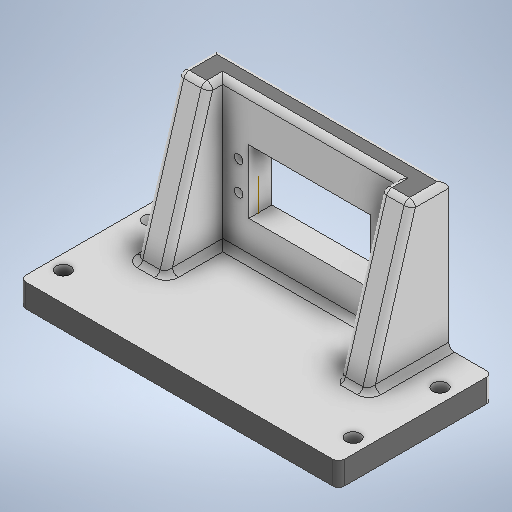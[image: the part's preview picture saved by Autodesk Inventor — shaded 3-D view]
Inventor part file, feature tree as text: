
AUTODESK INVENTOR PART (.ipt)
format: ipt  version: 2025.2 (Build 292293000, 293)  size: 492,032 bytes
history: native  units: mm
features: sketch x22, extrude x16, fillet x5, other x2, mirror x2, hole x1
ambient origin geometry x8: Origin, YZ Plane, XZ Plane, XY Plane, X Axis, Y Axis, Z Axis, Center Point
bodies: Body1 (feature_tree)
feature tree (48):
  other  "Bryła1"
  extrude  "Wyciągnięcie proste1"  Depth=110.0mm
  fillet  "Zaokrąglenie1"  Radius=90.0mm
  extrude  "Wyciągnięcie proste2"  Depth=8.0mm TaperAngle=0.0deg
  sketch  "Szkic8"
  sketch  "Szkic10"
  extrude  "Wyciągnięcie proste4"  Depth=2.0mm
  extrude  "Wyciągnięcie proste5"  Depth=22.0mm
  fillet  "Zaokrąglenie2"  Radius=22.0mm
  sketch  "Szkic15"
  sketch  "Szkic18"
  hole  "Otwór4"  [1 undecoded]
  extrude  "Wyciągnięcie proste10"  Depth=20.0mm
  mirror  "Odbij1"
  extrude  "Wyciągnięcie proste11"  Depth=10.0mm
  fillet  "Zaokrąglenie4"  Radius=20.0mm
  extrude  "Wyciągnięcie proste12"  Depth=64.0mm
  other  "Płaszczyzna konstrukcyjna1"
  extrude  "Wyciągnięcie proste13"  Depth=8.0mm
  extrude  "Wyciągnięcie proste14"  Depth=50.0mm TaperAngle=0.0deg
  sketch  "Szkic27"
  extrude  "Wyciągnięcie proste15"  Depth=20.0mm TaperAngle=0.0deg
  extrude  "Wyciągnięcie proste16"  Depth=25.0mm TaperAngle=0.0deg
  extrude  "Wyciągnięcie proste17"  Depth=2.0mm
  extrude  "Wyciągnięcie proste18"  Depth=5.0mm
  extrude  "Wyciągnięcie proste19"  Depth=5.0mm
  extrude  "Wyciągnięcie proste20"  Depth=5.0mm
  mirror  "Odbij5"
  extrude  "Wyciągnięcie proste21"  Depth=40.0mm
  fillet  "Zaokrąglenie7"  Radius=5.0mm
  fillet  "Zaokrąglenie8"  Radius=5.0mm
  sketch  "Szkic1"
  sketch  "Szkic5"
  sketch  "Szkic13"
  sketch  "Szkic14"
  sketch  "Szkic20"
  sketch  "Szkic22"
  sketch  "Szkic23"
  sketch  "Szkic24"
  sketch  "Szkic25"
  sketch  "Szkic26"
  sketch  "Szkic28"
  sketch  "Szkic29"
  sketch  "Szkic30"
  sketch  "Szkic31"
  sketch  "Szkic32"
  sketch  "Szkic33"
  sketch  "Szkic34"
note: 1 required parameter value undecoded (feature->parameter linkage not recoverable at this tier; creation-order binding heuristic only, values carry confidence <= 0.55)
